# Revit family: Legrand Marina version vitrée références 036927 à 036974
name_source: partatom
category: Installations électriques
revit_build: Autodesk Revit 2018 (Build: 20170223_1515(x64)
units: mm (PartAtom-declared; Revit-internal decimal feet)

## family parameters
Basée sur le plan de construction = Non
Conserver l'orientation des annotations = Non
Cote de connecteur circulaire = Utiliser le diamètre
Couper avec des vides une fois chargée = Non
Numéro OmniClass = 23.80.00.00
Partagée = Non
Point de calcul de pièce = Non
Titre OmniClass = Electric Power and Lighting
Toujours verticalement = Oui
Type d'élément = Normal

## types (12) — shared parameters
Conditions Générale d'Utilisation = https://export.legrand.com
ETIM Class = EC000058
Fabricant = Legrand
IK = 10
IP = 66
Matière = Métal
Nombre de porte = 1
Porte vitrée = Oui
RAL = 7035
URL = www.legrand.fr
Version horizontale = Non

## per-type parameters (varying)
| type | Coffret 036927 | Coffret 036928 | Coffret 036929 | Coffret 036936 | Coffret 036940 | Coffret 036941 | Coffret 036947 | Coffret 036948 | Coffret 036949 | Coffret 036956 | Coffret 036960 | Coffret 036974 | Hauteur | Longueur | Poids | Version carrée | Version verticale | profondeur |
| Legrand Atlantic 036927 | Oui | Non | Non | Non | Non | Non | Non | Non | Non | Non | Non | Non | 400 mm  [stored 1.31234 ft] | 300 mm  [stored 0.984252 ft] | 6.90 kg | Non | Oui | 200 mm  [stored 0.656168 ft] |
| Legrand Atlantic 036928 | Non | Oui | Non | Non | Non | Non | Non | Non | Non | Non | Non | Non | 500 mm  [stored 1.64042 ft] | 400 mm  [stored 1.31234 ft] | 11.20 kg | Non | Oui | 200 mm  [stored 0.656168 ft] |
| Legrand Atlantic 036929 | Non | Non | Oui | Non | Non | Non | Non | Non | Non | Non | Non | Non | 600 mm | 400 mm  [stored 1.31234 ft] | 13.00 kg | Non | Oui | 200 mm  [stored 0.656168 ft] |
| Legrand Atlantic 036936 | Non | Non | Non | Oui | Non | Non | Non | Non | Non | Non | Non | Non | 600 mm | 400 mm  [stored 1.31234 ft] | 14.00 kg | Non | Oui | 250 mm  [stored 0.82021 ft] |
| Legrand Atlantic 036940 | Non | Non | Non | Non | Oui | Non | Non | Non | Non | Non | Non | Non | 700 mm  [stored 2.29659 ft] | 500 mm  [stored 1.64042 ft] | 23.80 kg | Non | Oui | 250 mm  [stored 0.82021 ft] |
| Legrand Atlantic 036941 | Non | Non | Non | Non | Non | Oui | Non | Non | Non | Non | Non | Non | 800 mm  [stored 2.62467 ft] | 600 mm | 30.90 kg | Non | Oui | 250 mm  [stored 0.82021 ft] |
| Legrand Atlantic 036947 | Non | Non | Non | Non | Non | Non | Oui | Non | Non | Non | Non | Non | 800 mm  [stored 2.62467 ft] | 600 mm | 32.00 kg | Non | Oui | 300 mm  [stored 0.984252 ft] |
| Legrand Atlantic 036948 | Non | Non | Non | Non | Non | Non | Non | Oui | Non | Non | Non | Non | 1000 mm  [stored 3.28084 ft] | 600 mm | 45.00 kg | Non | Oui | 300 mm  [stored 0.984252 ft] |
| Legrand Atlantic 036949 | Non | Non | Non | Non | Non | Non | Non | Non | Oui | Non | Non | Non | 1000 mm  [stored 3.28084 ft] | 800 mm  [stored 2.62467 ft] | 56.90 kg | Non | Oui | 300 mm  [stored 0.984252 ft] |
| Legrand Atlantic 036956 | Non | Non | Non | Non | Non | Non | Non | Non | Non | Oui | Non | Non | 1200 mm | 800 mm  [stored 2.62467 ft] | 73.60 kg | Non | Oui | 400 mm  [stored 1.31234 ft] |
| Legrand Atlantic 036960 | Non | Non | Non | Non | Non | Non | Non | Non | Non | Non | Oui | Non | 1400 mm  [stored 4.59318 ft] | 800 mm  [stored 2.62467 ft] | 81.60 kg | Non | Oui | 400 mm  [stored 1.31234 ft] |
| Legrand Atlantic 036974 | Non | Non | Non | Non | Non | Non | Non | Non | Non | Non | Non | Oui | 600 mm | 600 mm | 22.80 kg | Oui | Non | 250 mm  [stored 0.82021 ft] |

note: [stored X ft] marks values corroborated as IEEE doubles in the binary element streams (Revit-internal decimal feet)
